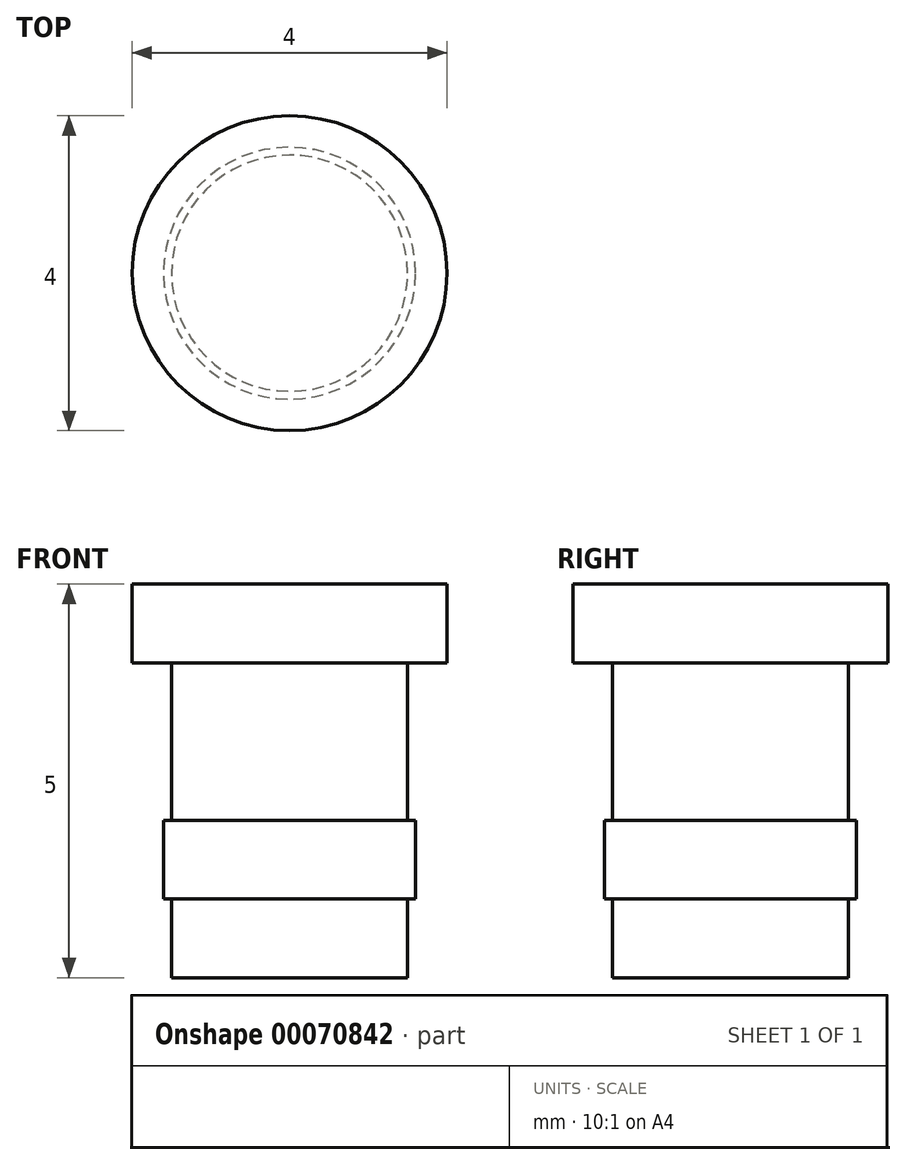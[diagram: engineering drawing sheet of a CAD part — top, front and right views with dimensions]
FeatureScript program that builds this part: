
annotation { "Feature Type Name" : "Feature", "Feature Type Description" : "" }
export const myFeature = defineFeature(function(context is Context, id is Id, definition is map)
    precondition{}
    {
        {
            var Q0;
            Q0=qCreatedBy(makeId("Front.planeOp"),FACE);
            var sketch = newSketch(context, id + "F0", { "sketchPlane" : qUnion([Q0])});
            skCircle(sketch, "E0", {"center": v(0, 0) * mm, "radius": 1.5 * mm});
            skCircle(sketch, "E1", {"center": v(0, 0) * mm, "radius": 2 * mm});
            skCircle(sketch, "E2", {"center": v(0, 0) * mm, "radius": 1.55 * mm});
            skSolve(sketch);
        }
        {
            var Q0;
            Q0=qCreatedBy(makeId("Right.planeOp"),FACE);
            var sketch = newSketch(context, id + "F1", { "sketchPlane" : qUnion([Q0])});
            skLineSegment(sketch, "E3", {"start": v(0, 0) * mm, "end": v(2, 0) * mm});
            skLineSegment(sketch, "E4", {"start": v(2, 0) * mm, "end": v(2, -1) * mm});
            skLineSegment(sketch, "E5", {"start": v(2, -1) * mm, "end": v(1.5, -1) * mm});
            skLineSegment(sketch, "E6", {"start": v(1.5, -1) * mm, "end": v(1.5, -3) * mm});
            skLineSegment(sketch, "E7", {"start": v(1.5, -3) * mm, "end": v(1.6, -3) * mm});
            skLineSegment(sketch, "E8", {"start": v(1.6, -3) * mm, "end": v(1.6, -4) * mm});
            skLineSegment(sketch, "E9", {"start": v(1.6, -4) * mm, "end": v(1.5, -4) * mm});
            skLineSegment(sketch, "E10", {"start": v(1.5, -4) * mm, "end": v(1.5, -5) * mm});
            skLineSegment(sketch, "E11", {"start": v(1.5, -5) * mm, "end": v(0, -5) * mm});
            skLineSegment(sketch, "E12", {"start": v(0, -5) * mm, "end": v(0, 0) * mm});
            skSolve(sketch);
        }
        {
            var Q0;
            Q0 = qSketchRegion(id + "F1", true);
            var Q1;
            Q1=sQuery(id+"F1.wireOp",EDGE,"E12");
            revolve(context, id + "F2", {"entities" : qUnion([Q0]), "axis" : qUnion([Q1]), "revolveType" : RevolveType.FULL});
        }
    });
